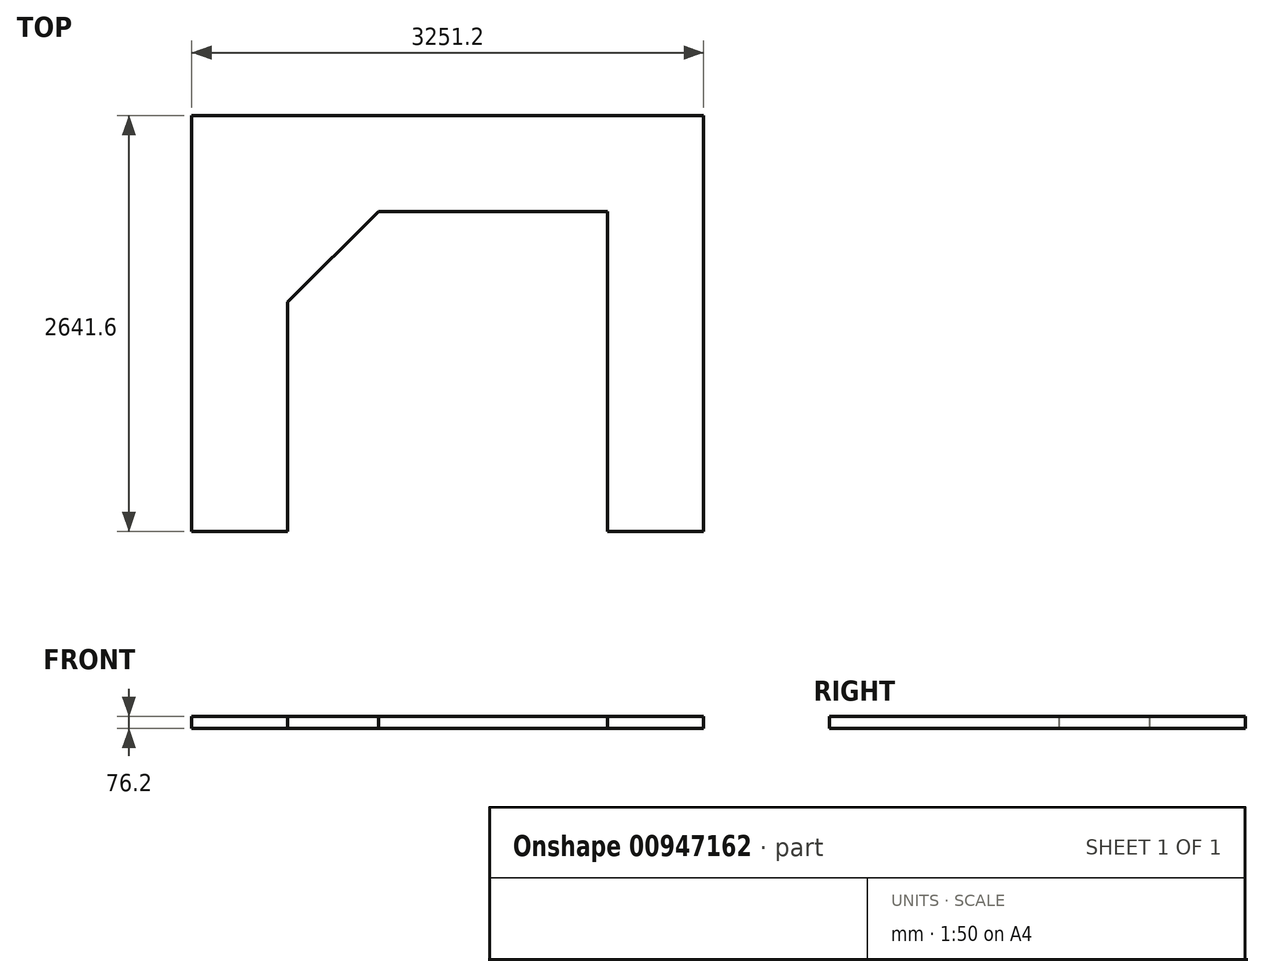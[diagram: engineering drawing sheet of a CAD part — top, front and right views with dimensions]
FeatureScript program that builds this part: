
annotation { "Feature Type Name" : "Feature", "Feature Type Description" : "" }
export const myFeature = defineFeature(function(context is Context, id is Id, definition is map)
    precondition{}
    {
        {
            var Q0;
            Q0=qCreatedBy(makeId("Top.planeOp"),FACE);
            var sketch = newSketch(context, id + "F0", { "sketchPlane" : qUnion([Q0])});
            skLineSegment(sketch, "E0.bottom", {"start": v(0, 0) * mm, "end": v(3251.2, 0) * mm});
            skLineSegment(sketch, "E0.top", {"start": v(0, 2641.6) * mm, "end": v(3251.2, 2641.6) * mm});
            skLineSegment(sketch, "E0.left", {"start": v(0, 0) * mm, "end": v(0, 2641.6) * mm});
            skLineSegment(sketch, "E0.right", {"start": v(3251.2, 0) * mm, "end": v(3251.2, 2641.6) * mm});
            skLineSegment(sketch, "E1", {"start": v(609.6, 0) * mm, "end": v(609.6, 1457.26) * mm});
            skLineSegment(sketch, "E2", {"start": v(609.6, 1457.26) * mm, "end": v(1184.34, 2032) * mm});
            skLineSegment(sketch, "E3", {"start": v(1184.34, 2032) * mm, "end": v(2641.6, 2032) * mm});
            skLineSegment(sketch, "E4", {"start": v(2641.6, 2032) * mm, "end": v(2641.6, 0) * mm});
            skSolve(sketch);
        }
        {
            var Q0;
            Q0=makeQuery(id+"F0.imprint","IMPRINT",FACE,{"disambiguationData":[TD([[makeQuery(id+"F0.imprint","IMPRINT",EDGE,{"derivedFrom":sQuery(id+"F0.wireOp",EDGE,"E0.top")}),-1.0]])]});
            extrude(context, id + "F1", {"entities" : qUnion([Q0]), "depth" : 76.2 * mm, "offsetDistance" : 25.4 * mm});
        }
    });
